# Revit family: ISI_IdealStandard_CounterTopWashbasins_CreateSquare_E3102
name_source: partatom
category: Plumbing Fixtures
revit_build: Autodesk Revit MEP 2012 (Build: 20110309_2315(x64)
units: mm (PartAtom-declared; Revit-internal decimal feet)

## types (1)
- E310201 - Create Square 50cm semi-countertop washbasin, 1 taphole with overflow, no chainstay hole
    Accessories = www.idealspec.co.uk
    AreaUnits = millimeters
    Assembly Code = C1030200
    AssetType = Fixed
    BIMObjectName = ISI_IdealStandard_CounterTopWashbasins_Profile21_E3102
    Brand = Ideal Standard
    CWFU = 0
    Category = SanitaryTerminal_WASHHANDBASIN_UK
    Color = White
    ConnectionType = Plumbing
    Default Elevation = 1219 mm
    Description = Create square 50 cm semi-countertop washbasin, 1 taphole with overflow, no chainstay hole
    DrainSize = 32 mm  [stored 0.104987 ft]
    DurationUnit = year
    ECA = No
    ExpectedLife = 30
    Features = 50 cm semi-countertop washbasin, 1 taphole with overflow, no chainstay hole
    Finish = White
    HWFU = 0
    IfcExportAs = IfcSanitaryTerminalType
    IfcExportType = WASHHANDBASIN
    InstallationInstructions = www.idealspec.co.uk/resources.html
    LinearUnits = millimeters
    ManufacturerURL = www.idealspec.co.uk
    Material = Vitreous china
    Model = E310201
    ModelNumber = E310201
    ModelReference = Create square 50 cm semi-countertop washbasin, 1 taphole with overflow, no chainstay hole
    NBSDescription = Counter top washbasins
    NBSReference = 45-35-70/360
    Name = CounterTopWashBasinsWASHHANDBASINS_ArmitageShanks_Profile21_E3102_IdealStandard
    NettWeight = 13.2 Kg
    NominalDepth = 455 mm
    NominalHeight = 200 mm  [stored 0.656168 ft]
    NominalLength = 455 mm
    NominalWidth = 500 mm
    ProductInformation = www.idealspec.co.uk/assets/datasheet/E310201
    Shape = Sculptured
    Size = 500 x 412 x 200 mm
    Space = Internal
    SpareParts = www.fastpart-spares.co.uk
    URL = www.idealspec.co.uk
    Uniclass2 = Pr_40_20_96_18
    Version = 2
    VolumeUnits = Litres
    WFU = 0
    WRAS = No
    WarrantyDescription = Manufacturers Warranty
    WarrantyDurationParts = 99
    WarrantyDurationUnit = year
    WashHandBasinMounting = CounterTop
    WashHandBasinType = HandRinse
    WaterEfficientProduct = No

note: [stored X ft] marks values corroborated as IEEE doubles in the binary element streams (Revit-internal decimal feet)

## geometry (parser evidence)
native form markers: Blend x2, Sweep x12
no freeform markers — native parametric forms only
